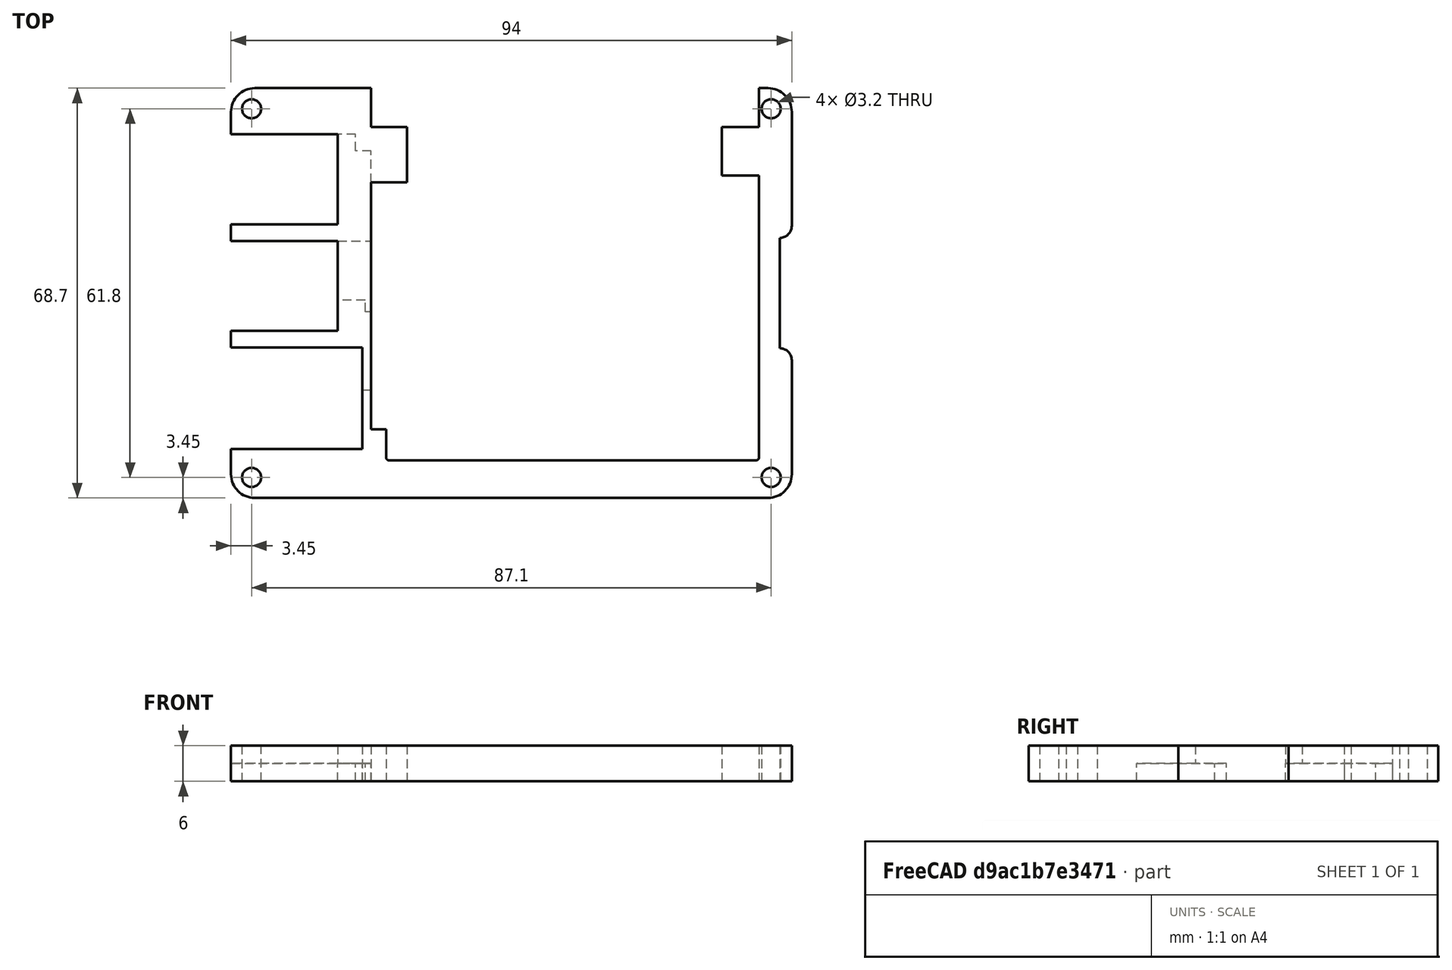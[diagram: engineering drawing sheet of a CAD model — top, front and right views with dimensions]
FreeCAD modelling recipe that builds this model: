
FCSTD DOCUMENT  (FreeCAD 0.19R24267 +148 (Git))
Label: 2. Lage
License: All rights reserved
LicenseURL: http://en.wikipedia.org/wiki/All_rights_reserved
objects: TechDraw::DrawViewDimension×23, Sketcher::SketchObject×3, TechDraw::DrawProjGroupItem×3, PartDesign::Pocket×2, PartDesign::Pad×1, PartDesign::Fillet×1, PartDesign::Body×1, TechDraw::DrawSVGTemplate×1, TechDraw::DrawProjGroup×1, TechDraw::DrawPage×1
note: 12 computed .brp shape members not serialized (recipe doc carries the construction recipe); baked Part::Feature solids carry a one-line shape summary decoded from their .brp

FEATURE [Sketcher::SketchObject] Sketch
  FullyConstrained = true
  MapMode = 5
  Support = -> [XY_Plane]
  sketch-geometry (9):
    g0: LineSegment StartX=0 StartY=0 StartZ=0 EndX=94 EndY=0 EndZ=0
    g1: LineSegment StartX=94 StartY=0 StartZ=0 EndX=94 EndY=68.7 EndZ=0
    g2: LineSegment StartX=94 StartY=68.7 StartZ=0 EndX=0 EndY=68.7 EndZ=0
    g3: LineSegment StartX=0 StartY=68.7 StartZ=0 EndX=0 EndY=0 EndZ=0
    g4: GeomPoint X=47 Y=34.35 Z=0
    g5: Circle CenterX=3.45 CenterY=65.25 CenterZ=0 NormalX=0 NormalY=0 NormalZ=1 AngleXU=0 Radius=1.6
    g6: Circle CenterX=90.55 CenterY=65.25 CenterZ=0 NormalX=0 NormalY=0 NormalZ=1 AngleXU=0 Radius=1.6
    g7: Circle CenterX=90.55 CenterY=3.45 CenterZ=0 NormalX=0 NormalY=0 NormalZ=1 AngleXU=0 Radius=1.6
    g8: Circle CenterX=3.45 CenterY=3.45 CenterZ=0 NormalX=0 NormalY=0 NormalZ=1 AngleXU=0 Radius=1.6
  constraints (22):
    c: Coincident(g0,g1)
    c: Coincident(g1,g2)
    c: Coincident(g2,g3)
    c: Coincident(g3,g0)
    c: Horizontal(g0)
    c: Horizontal(g2)
    c: Vertical(g1)
    c: Vertical(g3)
    c: Coincident(g0,g-1)
    c: DistanceX(g2,g2) = 94
    c: DistanceY(g3,g3) = 68.7
    c: Symmetric(g2,g0,g4)
    c: Equal(g8,g5)
    c: Equal(g5,g6)
    c: Equal(g6,g7)
    c: Symmetric(g8,g6,g4)
    c: Symmetric(g5,g7,g4)
    c: Radius(g7) = 1.6
    c: Vertical(g8,g5)
    c: Horizontal(g8,g7)
    c: DistanceY(g0,g8) = 3.45
    c: DistanceX(g0,g8) = 3.45
FEATURE [PartDesign::Pad] Pad
  Direction = (1,1,1)
  Length = 6
  Length2 = 100
  Profile = -> Sketch
  Type = 0
FEATURE [Sketcher::SketchObject] Sketch001
  ExternalGeometry = -> [Pad]
  FullyConstrained = true
  MapMode = 5
  Placement = pos=(0,0,6) rot=(0,0,1;0rad)
  Support = -> [Pad]
  sketch-geometry (33):
    g0: LineSegment StartX=0 StartY=8.2 StartZ=0 EndX=22 EndY=8.2 EndZ=0
    g1: LineSegment StartX=22 StartY=8.2 StartZ=0 EndX=22 EndY=25.2 EndZ=0
    g2: LineSegment StartX=22 StartY=25.2 StartZ=0 EndX=0 EndY=25.2 EndZ=0
    g3: LineSegment StartX=0 StartY=25.2 StartZ=0 EndX=0 EndY=8.2 EndZ=0
    g4: LineSegment StartX=0 StartY=28 StartZ=0 EndX=17.9 EndY=28 EndZ=0
    g5: LineSegment StartX=17.9 StartY=28 StartZ=0 EndX=17.9 EndY=43.1 EndZ=0
    g6: LineSegment StartX=17.9 StartY=43.1 StartZ=0 EndX=0 EndY=43.1 EndZ=0
    g7: LineSegment StartX=0 StartY=43.1 StartZ=0 EndX=0 EndY=28 EndZ=0
    g8: LineSegment StartX=0 StartY=45.9 StartZ=0 EndX=17.9 EndY=45.9 EndZ=0
    g9: LineSegment StartX=17.9 StartY=45.9 StartZ=0 EndX=17.9 EndY=61 EndZ=0
    g10: LineSegment StartX=17.9 StartY=61 StartZ=0 EndX=0 EndY=61 EndZ=0
    g11: LineSegment StartX=0 StartY=61 StartZ=0 EndX=0 EndY=45.9 EndZ=0
    g12: LineSegment StartX=92 StartY=43.6 StartZ=0 EndX=92 EndY=25.1 EndZ=0
    g13: ArcOfCircle CenterX=92 CenterY=23.1 CenterZ=0 NormalX=0 NormalY=0 NormalZ=1 AngleXU=0 Radius=2 StartAngle=0 EndAngle=1.5708
    g14: ArcOfCircle CenterX=92 CenterY=45.6 CenterZ=0 NormalX=0 NormalY=0 NormalZ=1 AngleXU=0 Radius=2 StartAngle=4.71239 EndAngle=6.28319
    g15: GeomPoint X=94 Y=34.35 Z=0
    g16: LineSegment StartX=88.5 StartY=68.7 StartZ=0 EndX=88.5 EndY=62.2 EndZ=0
    g17: LineSegment StartX=88.5 StartY=62.2 StartZ=0 EndX=82.3 EndY=62.2 EndZ=0
    g18: LineSegment StartX=82.3 StartY=62.2 StartZ=0 EndX=82.3 EndY=54.05 EndZ=0
    g19: LineSegment StartX=82.3 StartY=54.05 StartZ=0 EndX=88.5 EndY=54.05 EndZ=0
    g20: LineSegment StartX=88.5 StartY=54.05 StartZ=0 EndX=88.5 EndY=6.8 EndZ=0
    g21: ArcOfCircle CenterX=88 CenterY=6.8 CenterZ=0 NormalX=0 NormalY=0 NormalZ=1 AngleXU=0 Radius=0.5 StartAngle=4.71239 EndAngle=6.28319
    g22: LineSegment StartX=88 StartY=6.3 StartZ=0 EndX=26.5 EndY=6.3 EndZ=0
    g23: ArcOfCircle CenterX=26.5 CenterY=6.8 CenterZ=0 NormalX=0 NormalY=0 NormalZ=1 AngleXU=0 Radius=0.5 StartAngle=3.14159 EndAngle=4.71239
    g24: LineSegment StartX=26 StartY=6.8 StartZ=0 EndX=26 EndY=11.5 EndZ=0
    g25: LineSegment StartX=26 StartY=11.5 StartZ=0 EndX=23.5 EndY=11.5 EndZ=0
    g26: LineSegment StartX=23.5 StartY=11.5 StartZ=0 EndX=23.5 EndY=52.9 EndZ=0
    g27: LineSegment StartX=23.5 StartY=52.9 StartZ=0 EndX=29.5 EndY=52.9 EndZ=0
    g28: LineSegment StartX=29.5 StartY=52.9 StartZ=0 EndX=29.5 EndY=62.2 EndZ=0
    g29: LineSegment StartX=29.5 StartY=62.2 StartZ=0 EndX=23.5 EndY=62.2 EndZ=0
    g30: LineSegment StartX=23.5 StartY=62.2 StartZ=0 EndX=23.5 EndY=68.7 EndZ=0
    g31: LineSegment StartX=23.5 StartY=68.7 StartZ=0 EndX=88.5 EndY=68.7 EndZ=0
    g32: LineSegment StartX=94 StartY=23.1 StartZ=0 EndX=94 EndY=45.6 EndZ=0
  constraints (96):
    c: Coincident(g0,g1)
    c: Coincident(g1,g2)
    c: Coincident(g2,g3)
    c: Coincident(g3,g0)
    c: Horizontal(g0)
    c: Horizontal(g2)
    c: Vertical(g1)
    c: Vertical(g3)
    c: PointOnObject(g0,g-3)
    c: Coincident(g4,g5)
    c: Coincident(g5,g6)
    c: Coincident(g6,g7)
    c: Coincident(g7,g4)
    c: Horizontal(g4)
    c: Horizontal(g6)
    c: Vertical(g5)
    c: Vertical(g7)
    c: PointOnObject(g4,g-3)
    c: Coincident(g8,g9)
    c: Coincident(g9,g10)
    c: Coincident(g10,g11)
    c: Coincident(g11,g8)
    c: Horizontal(g8)
    c: Horizontal(g10)
    c: Vertical(g9)
    c: Vertical(g11)
    c: PointOnObject(g8,g-3)
    c: Vertical(g8,g5)
    c: DistanceY(g1,g4) = 2.8
    c: DistanceY(g1,g1) = 17
    c: DistanceY(g-1,g0) = 8.2
    c: Equal(g5,g9)
    c: DistanceY(g5,g5) = 15.1
    c: DistanceY(g5,g8) = 2.8
    c: DistanceX(g4,g4) = 17.9
    c: DistanceX(g0,g0) = 22
    c: Vertical(g12)
    c: Perpendicular(g12,g13) = 4.71239
    c: Perpendicular(g12,g14) = 1.5708
    c: PointOnObject(g14,g-5)
    c: Horizontal(g14,g14)
    c: Horizontal(g13,g13)
    c: Symmetric(g13,g14,g15)
    c: Symmetric(g-6,g-5,g15)
    c: Radius(g13) = 2
    c: DistanceY(g12,g12) = 18.5
    c: PointOnObject(g16,g-4)
    c: Vertical(g16)
    c: Coincident(g16,g17)
    c: Horizontal(g17)
    c: Coincident(g17,g18)
    c: Vertical(g18)
    c: Coincident(g18,g19)
    c: Horizontal(g19)
    c: Coincident(g19,g20)
    c: Vertical(g20)
    c: Tangent(g20,g21) = 1.5708
    c: Coincident(g21,g22)
    c: Horizontal(g22)
    c: Tangent(g22,g23) = 1.5708
    c: Coincident(g23,g24)
    c: Vertical(g24)
    c: Coincident(g24,g25)
    c: Horizontal(g25)
    c: Coincident(g25,g26)
    c: Vertical(g26)
    c: Coincident(g26,g27)
    c: Horizontal(g27)
    c: Coincident(g27,g28)
    c: Vertical(g28)
    c: Coincident(g28,g29)
    c: Horizontal(g29)
    c: Coincident(g29,g30)
    c: PointOnObject(g30,g-4)
    c: Vertical(g30)
    c: Vertical(g29,g26)
    c: Vertical(g16,g19)
    c: Vertical(g21,g21)
    c: Horizontal(g23,g23)
    c: Horizontal(g23,g21)
    c: Radius(g21) = 0.5
    c: Horizontal(g17,g28)
    c: DistanceY(g16,g16) = 6.5
    c: DistanceX(g19,g-5) = 5.5
    c: DistanceY(g18,g18) = 8.15
    c: DistanceX(g17,g-5) = 11.7
    c: DistanceY(g-6,g22) = 6.3
    c: DistanceX(g29,g29) = 6
    c: DistanceX(g25,g20) = 65
    c: DistanceX(g25,g22) = 3
    c: DistanceY(g-1,g25) = 11.5
    c: Coincident(g31,g30)
    c: Coincident(g31,g16)
    c: DistanceY(g28,g28) = 9.3
    c: Coincident(g32,g13)
    c: Coincident(g32,g14)
FEATURE [PartDesign::Pocket] Pocket
  BaseFeature = -> Pad
  Length = 6
  Length2 = 100
  Profile = -> Sketch001
  Type = 0
FEATURE [Sketcher::SketchObject] Sketch002
  ExternalGeometry = -> [Pocket]
  FullyConstrained = true
  MapMode = 5
  Placement = pos=(0,0,0) rot=(1,0,0;3.14159rad)
  Support = -> [Pocket]
  sketch-geometry (18):
    g0: LineSegment StartX=22 StartY=-18.1 StartZ=0 EndX=23.5 EndY=-18.1 EndZ=0
    g1: LineSegment StartX=23.5 StartY=-18.1 StartZ=0 EndX=23.5 EndY=-31.2 EndZ=0
    g2: LineSegment StartX=23.5 StartY=-31.2 StartZ=0 EndX=22.5 EndY=-31.2 EndZ=0
    g3: LineSegment StartX=22.5 StartY=-31.2 StartZ=0 EndX=22.5 EndY=-33.2 EndZ=0
    g4: LineSegment StartX=22.5 StartY=-33.2 StartZ=0 EndX=17.9 EndY=-33.2 EndZ=0
    g5: LineSegment StartX=17.9 StartY=-33.2 StartZ=0 EndX=17.9 EndY=-28 EndZ=0
    g6: LineSegment StartX=17.9 StartY=-28 StartZ=0 EndX=0 EndY=-28 EndZ=0
    g7: LineSegment StartX=0 StartY=-28 StartZ=0 EndX=0 EndY=-25.2 EndZ=0
    g8: LineSegment StartX=0 StartY=-25.2 StartZ=0 EndX=22 EndY=-25.2 EndZ=0
    g9: LineSegment StartX=22 StartY=-25.2 StartZ=0 EndX=22 EndY=-18.1 EndZ=0
    g10: LineSegment StartX=0 StartY=-43.1 StartZ=0 EndX=23.5 EndY=-43.1 EndZ=0
    g11: LineSegment StartX=23.5 StartY=-43.1 StartZ=0 EndX=23.5 EndY=-58.2 EndZ=0
    g12: LineSegment StartX=23.5 StartY=-58.2 StartZ=0 EndX=20.9 EndY=-58.2 EndZ=0
    g13: LineSegment StartX=20.9 StartY=-58.2 StartZ=0 EndX=20.9 EndY=-61 EndZ=0
    g14: LineSegment StartX=20.9 StartY=-61 StartZ=0 EndX=17.9 EndY=-61 EndZ=0
    g15: LineSegment StartX=17.9 StartY=-61 StartZ=0 EndX=17.9 EndY=-45.9 EndZ=0
    g16: LineSegment StartX=17.9 StartY=-45.9 StartZ=0 EndX=0 EndY=-45.9 EndZ=0
    g17: LineSegment StartX=0 StartY=-45.9 StartZ=0 EndX=0 EndY=-43.1 EndZ=0
  constraints (49):
    c: PointOnObject(g0,g-7)
    c: PointOnObject(g0,g-5)
    c: Horizontal(g0)
    c: DistanceY(g0,g-5) = 6.6
    c: Coincident(g0,g1)
    c: PointOnObject(g1,g-5)
    c: Coincident(g1,g2)
    c: Horizontal(g2)
    c: Coincident(g2,g3)
    c: Vertical(g3)
    c: Coincident(g3,g4)
    c: PointOnObject(g4,g-12)
    c: Horizontal(g4)
    c: Coincident(g4,g5)
    c: Coincident(g5,g-12)
    c: Coincident(g6,g7)
    c: Coincident(g7,g-6)
    c: Coincident(g7,g8)
    c: Coincident(g8,g-7)
    c: Coincident(g8,g9)
    c: Coincident(g9,g0)
    c: Coincident(g6,g5)
    c: Horizontal(g6)
    c: Vertical(g7)
    c: DistanceY(g-9,g1) = 37.5
    c: DistanceX(g2,g2) = 1
    c: DistanceY(g3,g3) = 2
    c: PointOnObject(g10,g-2)
    c: PointOnObject(g10,g-5)
    c: Horizontal(g10)
    c: Coincident(g10,g11)
    c: Vertical(g11)
    c: Coincident(g11,g12)
    c: Horizontal(g12)
    c: Coincident(g12,g13)
    c: Vertical(g13)
    c: Coincident(g13,g14)
    c: Coincident(g14,g-10)
    c: Horizontal(g14)
    c: Coincident(g14,g15)
    c: Coincident(g15,g-10)
    c: Coincident(g15,g16)
    c: PointOnObject(g16,g-2)
    c: Horizontal(g16)
    c: Coincident(g16,g17)
    c: Coincident(g17,g10)
    c: Horizontal(g10,g-12)
    c: DistanceY(g-9,g12) = 10.5
    c: DistanceX(g14,g14) = 3
FEATURE [PartDesign::Pocket] Pocket001
  BaseFeature = -> Pocket
  Length = 3
  Length2 = 100
  Profile = -> Sketch002
  Type = 0
FEATURE [PartDesign::Fillet] Fillet
  Base = -> Pocket001 [Edge123,Edge1,Edge2,Edge94]
  BaseFeature = -> Pocket001
  Radius = 4
  SupportTransform = false
FEATURE [PartDesign::Body] Body
  Group = -> [Sketch,Pad,Sketch001,Pocket,Sketch002,Pocket001,Fillet]
  Origin = -> Origin
  Tip = -> Fillet
FEATURE [TechDraw::DrawSVGTemplate] Template
  EditableTexts = Designed_by_Name=David Völlm; Drawing_number=Drawing number; FC-Date=23.05.2023; FC-SC=1:2; FC-SH=Sheet; FC-Title=2. Lage; Subtitle=Subtitle; Weight=Weight
  Height = 210
  Orientation = 1
  Width = 297
FEATURE [TechDraw::DrawProjGroupItem] ProjItem  label="Front"
  CoarseView = false
  Direction = (0,0,-1)
  Focus = 100
  HardHidden = false
  IsoCount = 0
  IsoHidden = false
  IsoVisible = false
  LockPosition = true
  Perspective = false
  Rotation = 0
  RotationVector = (1,0,0)
  Scale = 0.5
  ScaleType = 2
  SeamHidden = false
  SeamVisible = true
  SmoothHidden = false
  SmoothVisible = true
  Source = -> [Body]
  Type = 0
  X = 0
  XDirection = (1,0,0)
  Y = 0
FEATURE [TechDraw::DrawProjGroupItem] ProjItem001  label="Left"
  CoarseView = false
  Direction = (-1,0,-1e-16)
  Focus = 100
  HardHidden = false
  IsoCount = 0
  IsoHidden = false
  IsoVisible = false
  LockPosition = false
  Perspective = false
  Rotation = 0
  RotationVector = (1,0,0)
  Scale = 0.5
  ScaleType = 2
  SeamHidden = false
  SeamVisible = true
  SmoothHidden = false
  SmoothVisible = true
  Source = -> [Body]
  Type = 1
  X = 87.187
  XDirection = (1e-16,0,-1)
  Y = 0
FEATURE [TechDraw::DrawProjGroupItem] ProjItem002  label="Bottom"
  CoarseView = false
  Direction = (0,1,0)
  Focus = 100
  HardHidden = false
  IsoCount = 0
  IsoHidden = false
  IsoVisible = false
  LockPosition = false
  Perspective = false
  Rotation = 0
  RotationVector = (1,0,0)
  Scale = 0.5
  ScaleType = 2
  SeamHidden = false
  SeamVisible = true
  SmoothHidden = false
  SmoothVisible = true
  Source = -> [Body]
  Type = 5
  X = 0
  XDirection = (1,0,0)
  Y = 60.2874
FEATURE [TechDraw::DrawProjGroup] ProjGroup
  Anchor = -> ProjItem
  AutoDistribute = true
  LockPosition = false
  ProjectionType = 0
  Rotation = 0
  Scale = 0.5
  ScaleType = 2
  Source = -> [Body]
  Views = -> [ProjItem,ProjItem001,ProjItem002]
  X = 77.6724
  Y = 92.6298
  spacingX = 15
  spacingY = 15
FEATURE [TechDraw::DrawViewDimension] Dimension
  Arbitrary = false
  ArbitraryTolerances = false
  EqualTolerance = true
  FormatSpec = %.2f
  FormatSpecOverTolerance = %+.2f
  FormatSpecUnderTolerance = %+.2f
  Inverted = false
  LockPosition = false
  MeasureType = 1
  OverTolerance = 0
  References2D = -> [ProjItem]
  Rotation = 0
  ScaleType = 0
  TheoreticalExact = false
  Type = 1
  UnderTolerance = 0
  X = -33.4574
  Y = -14.7676
FEATURE [TechDraw::DrawViewDimension] Dimension001
  Arbitrary = false
  ArbitraryTolerances = false
  EqualTolerance = true
  FormatSpec = %.2f
  FormatSpecOverTolerance = %+.2f
  FormatSpecUnderTolerance = %+.2f
  Inverted = false
  LockPosition = false
  MeasureType = 1
  OverTolerance = 0
  References2D = -> [ProjItem]
  Rotation = 0
  ScaleType = 0
  TheoreticalExact = false
  Type = 1
  UnderTolerance = 0
  X = -33.8024
  Y = -22.3927
FEATURE [TechDraw::DrawViewDimension] Dimension002
  Arbitrary = false
  ArbitraryTolerances = false
  EqualTolerance = true
  FormatSpec = %.2f
  FormatSpecOverTolerance = %+.2f
  FormatSpecUnderTolerance = %+.2f
  Inverted = false
  LockPosition = false
  MeasureType = 1
  OverTolerance = 0
  References2D = -> [ProjItem]
  Rotation = 0
  ScaleType = 0
  TheoreticalExact = false
  Type = 1
  UnderTolerance = 0
  X = -34.2743
  Y = -28.3507
FEATURE [TechDraw::DrawViewDimension] Dimension003
  Arbitrary = false
  ArbitraryTolerances = false
  EqualTolerance = true
  FormatSpec = %.2f
  FormatSpecOverTolerance = %+.2f
  FormatSpecUnderTolerance = %+.2f
  Inverted = false
  LockPosition = false
  MeasureType = 1
  OverTolerance = 0
  References2D = -> [ProjItem]
  Rotation = 0
  ScaleType = 0
  TheoreticalExact = false
  Type = 1
  UnderTolerance = 0
  X = -34.985
  Y = -35.1901
FEATURE [TechDraw::DrawViewDimension] Dimension004
  Arbitrary = false
  ArbitraryTolerances = false
  EqualTolerance = true
  FormatSpec = %.2f
  FormatSpecOverTolerance = %+.2f
  FormatSpecUnderTolerance = %+.2f
  Inverted = false
  LockPosition = false
  MeasureType = 1
  OverTolerance = 0
  References2D = -> [ProjItem]
  Rotation = 0
  ScaleType = 0
  TheoreticalExact = false
  Type = 1
  UnderTolerance = 0
  X = -34.3611
  Y = -41.0321
FEATURE [TechDraw::DrawViewDimension] Dimension005
  Arbitrary = false
  ArbitraryTolerances = false
  EqualTolerance = true
  FormatSpec = %.2f
  FormatSpecOverTolerance = %+.2f
  FormatSpecUnderTolerance = %+.2f
  Inverted = false
  LockPosition = false
  MeasureType = 1
  OverTolerance = 0
  References2D = -> [ProjItem]
  Rotation = 0
  ScaleType = 0
  TheoreticalExact = false
  Type = 1
  UnderTolerance = 0
  X = -17.753
  Y = 23.9916
FEATURE [TechDraw::DrawViewDimension] Dimension006
  Arbitrary = false
  ArbitraryTolerances = false
  EqualTolerance = true
  FormatSpec = %.2f
  FormatSpecOverTolerance = %+.2f
  FormatSpecUnderTolerance = %+.2f
  Inverted = false
  LockPosition = false
  MeasureType = 1
  OverTolerance = 0
  References2D = -> [ProjItem]
  Rotation = 0
  ScaleType = 0
  TheoreticalExact = false
  Type = 1
  UnderTolerance = 0
  X = -11.0217
  Y = 30.8611
FEATURE [TechDraw::DrawViewDimension] Dimension007
  Arbitrary = false
  ArbitraryTolerances = false
  EqualTolerance = true
  FormatSpec = %.2f
  FormatSpecOverTolerance = %+.2f
  FormatSpecUnderTolerance = %+.2f
  Inverted = false
  LockPosition = false
  MeasureType = 1
  OverTolerance = 0
  References2D = -> [ProjItem]
  Rotation = 0
  ScaleType = 0
  TheoreticalExact = false
  Type = 1
  UnderTolerance = 0
  X = -5.15369
  Y = 43.0578
FEATURE [TechDraw::DrawViewDimension] Dimension008
  Arbitrary = false
  ArbitraryTolerances = false
  EqualTolerance = true
  FormatSpec = %.2f
  FormatSpecOverTolerance = %+.2f
  FormatSpecUnderTolerance = %+.2f
  Inverted = false
  LockPosition = false
  MeasureType = 1
  OverTolerance = 0
  References2D = -> [ProjItem]
  Rotation = 0
  ScaleType = 0
  TheoreticalExact = false
  Type = 1
  UnderTolerance = 0
  X = -3.6715
  Y = 36.8578
FEATURE [TechDraw::DrawViewDimension] Dimension009
  Arbitrary = false
  ArbitraryTolerances = false
  EqualTolerance = true
  FormatSpec = %.2f
  FormatSpecOverTolerance = %+.2f
  FormatSpecUnderTolerance = %+.2f
  Inverted = false
  LockPosition = false
  MeasureType = 1
  OverTolerance = 0
  References2D = -> [ProjItem]
  Rotation = 0
  ScaleType = 0
  TheoreticalExact = false
  Type = 1
  UnderTolerance = 0
  X = 30.5677
  Y = -17.1195
FEATURE [TechDraw::DrawViewDimension] Dimension010
  Arbitrary = false
  ArbitraryTolerances = false
  EqualTolerance = true
  FormatSpec = %.2f
  FormatSpecOverTolerance = %+.2f
  FormatSpecUnderTolerance = %+.2f
  Inverted = false
  LockPosition = false
  MeasureType = 1
  OverTolerance = 0
  References2D = -> [ProjItem]
  Rotation = 0
  ScaleType = 0
  TheoreticalExact = false
  Type = 1
  UnderTolerance = 0
  X = 32.6884
  Y = -23.1762
FEATURE [TechDraw::DrawViewDimension] Dimension011
  Arbitrary = false
  ArbitraryTolerances = false
  EqualTolerance = true
  FormatSpec = %.2f
  FormatSpecOverTolerance = %+.2f
  FormatSpecUnderTolerance = %+.2f
  Inverted = false
  LockPosition = false
  MeasureType = 1
  OverTolerance = 0
  References2D = -> [ProjItem]
  Rotation = 0
  ScaleType = 0
  TheoreticalExact = false
  Type = 2
  UnderTolerance = 0
  X = 40.4801
  Y = -21.6067
FEATURE [TechDraw::DrawViewDimension] Dimension012
  Arbitrary = false
  ArbitraryTolerances = false
  EqualTolerance = true
  FormatSpec = %.2f
  FormatSpecOverTolerance = %+.2f
  FormatSpecUnderTolerance = %+.2f
  Inverted = false
  LockPosition = false
  MeasureType = 1
  OverTolerance = 0
  References2D = -> [ProjItem]
  Rotation = 0
  ScaleType = 0
  TheoreticalExact = false
  Type = 2
  UnderTolerance = 0
  X = 38.0926
  Y = -8.64696
FEATURE [TechDraw::DrawViewDimension] Dimension013
  Arbitrary = false
  ArbitraryTolerances = false
  EqualTolerance = true
  FormatSpec = %.2f
  FormatSpecOverTolerance = %+.2f
  FormatSpecUnderTolerance = %+.2f
  Inverted = false
  LockPosition = false
  MeasureType = 1
  OverTolerance = 0
  References2D = -> [ProjItem]
  Rotation = 0
  ScaleType = 0
  TheoreticalExact = false
  Type = 2
  UnderTolerance = 0
  X = 49.3389
  Y = -9.70702
FEATURE [TechDraw::DrawViewDimension] Dimension014
  Arbitrary = false
  ArbitraryTolerances = false
  EqualTolerance = true
  FormatSpec = %.2f
  FormatSpecOverTolerance = %+.2f
  FormatSpecUnderTolerance = %+.2f
  Inverted = false
  LockPosition = false
  MeasureType = 1
  OverTolerance = 0
  References2D = -> [ProjItem]
  Rotation = 0
  ScaleType = 0
  TheoreticalExact = false
  Type = 1
  UnderTolerance = 0
  X = 8.1351
  Y = 5.93015
FEATURE [TechDraw::DrawViewDimension] Dimension015
  Arbitrary = false
  ArbitraryTolerances = false
  EqualTolerance = true
  FormatSpec = %.2f
  FormatSpecOverTolerance = %+.2f
  FormatSpecUnderTolerance = %+.2f
  Inverted = false
  LockPosition = false
  MeasureType = 1
  OverTolerance = 0
  References2D = -> [ProjItem]
  Rotation = 0
  ScaleType = 0
  TheoreticalExact = false
  Type = 1
  UnderTolerance = 0
  X = 7.3881
  Y = 0.370228
FEATURE [TechDraw::DrawViewDimension] Dimension016
  Arbitrary = false
  ArbitraryTolerances = false
  EqualTolerance = true
  FormatSpec = %.2f
  FormatSpecOverTolerance = %+.2f
  FormatSpecUnderTolerance = %+.2f
  Inverted = false
  LockPosition = false
  MeasureType = 1
  OverTolerance = 0
  References2D = -> [ProjItem]
  Rotation = 0
  ScaleType = 0
  TheoreticalExact = false
  Type = 2
  UnderTolerance = 0
  X = 33.336
  Y = 1.32146
FEATURE [TechDraw::DrawViewDimension] Dimension017
  Arbitrary = false
  ArbitraryTolerances = false
  EqualTolerance = true
  FormatSpec = %.2f
  FormatSpecOverTolerance = %+.2f
  FormatSpecUnderTolerance = %+.2f
  Inverted = false
  LockPosition = false
  MeasureType = 1
  OverTolerance = 0
  References2D = -> [ProjItem]
  Rotation = 0
  ScaleType = 0
  TheoreticalExact = false
  Type = 2
  UnderTolerance = 0
  X = 46.522
  Y = 1.9535
FEATURE [TechDraw::DrawViewDimension] Dimension018
  Arbitrary = false
  ArbitraryTolerances = false
  EqualTolerance = true
  FormatSpec = %.2f
  FormatSpecOverTolerance = %+.2f
  FormatSpecUnderTolerance = %+.2f
  Inverted = false
  LockPosition = false
  MeasureType = 1
  OverTolerance = 0
  References2D = -> [ProjItem]
  Rotation = 0
  ScaleType = 0
  TheoreticalExact = false
  Type = 2
  UnderTolerance = 0
  X = 40.8683
  Y = 13.25
FEATURE [TechDraw::DrawViewDimension] Dimension019
  Arbitrary = false
  ArbitraryTolerances = false
  EqualTolerance = true
  FormatSpec = R%.2f
  FormatSpecOverTolerance = %+.2f
  FormatSpecUnderTolerance = %+.2f
  Inverted = false
  LockPosition = false
  MeasureType = 1
  OverTolerance = 0
  References2D = -> [ProjItem]
  Rotation = 0
  ScaleType = 0
  TheoreticalExact = false
  Type = 4
  UnderTolerance = 0
  X = 39.8086
  Y = 40.3113
FEATURE [TechDraw::DrawViewDimension] Dimension020
  Arbitrary = false
  ArbitraryTolerances = false
  EqualTolerance = true
  FormatSpec = R%.2f
  FormatSpecOverTolerance = %+.2f
  FormatSpecUnderTolerance = %+.2f
  Inverted = false
  LockPosition = false
  MeasureType = 1
  OverTolerance = 0
  References2D = -> [ProjItem]
  Rotation = 0
  ScaleType = 0
  TheoreticalExact = false
  Type = 4
  UnderTolerance = 0
  X = 39.4065
  Y = 27.3433
FEATURE [TechDraw::DrawViewDimension] Dimension021
  Arbitrary = false
  ArbitraryTolerances = false
  EqualTolerance = true
  FormatSpec = %.2f
  FormatSpecOverTolerance = %+.2f
  FormatSpecUnderTolerance = %+.2f
  Inverted = false
  LockPosition = false
  MeasureType = 1
  OverTolerance = 0
  References2D = -> [ProjItem001]
  Rotation = 0
  ScaleType = 0
  TheoreticalExact = false
  Type = 1
  UnderTolerance = 0
  X = -9.94797
  Y = -23.7488
FEATURE [TechDraw::DrawViewDimension] Dimension022
  Arbitrary = false
  ArbitraryTolerances = false
  EqualTolerance = true
  FormatSpec = %.2f
  FormatSpecOverTolerance = %+.2f
  FormatSpecUnderTolerance = %+.2f
  Inverted = false
  LockPosition = false
  MeasureType = 1
  OverTolerance = 0
  References2D = -> [ProjItem001]
  Rotation = 0
  ScaleType = 0
  TheoreticalExact = false
  Type = 1
  UnderTolerance = 0
  X = -10.4071
  Y = -13.9101
FEATURE [TechDraw::DrawPage] Page
  KeepUpdated = true
  NextBalloonIndex = 1
  ProjectionType = 0
  Template = -> Template
  Views = -> [ProjGroup,Dimension,Dimension001,Dimension002,Dimension003,Dimension004,Dimension005,Dimension006,Dimension007,Dimension008,Dimension009,Dimension010,Dimension011,Dimension012,Dimension013,Dimension014,Dimension015,Dimension016,Dimension017,Dimension018,Dimension019,Dimension020,Dimension021,Dimension022]
